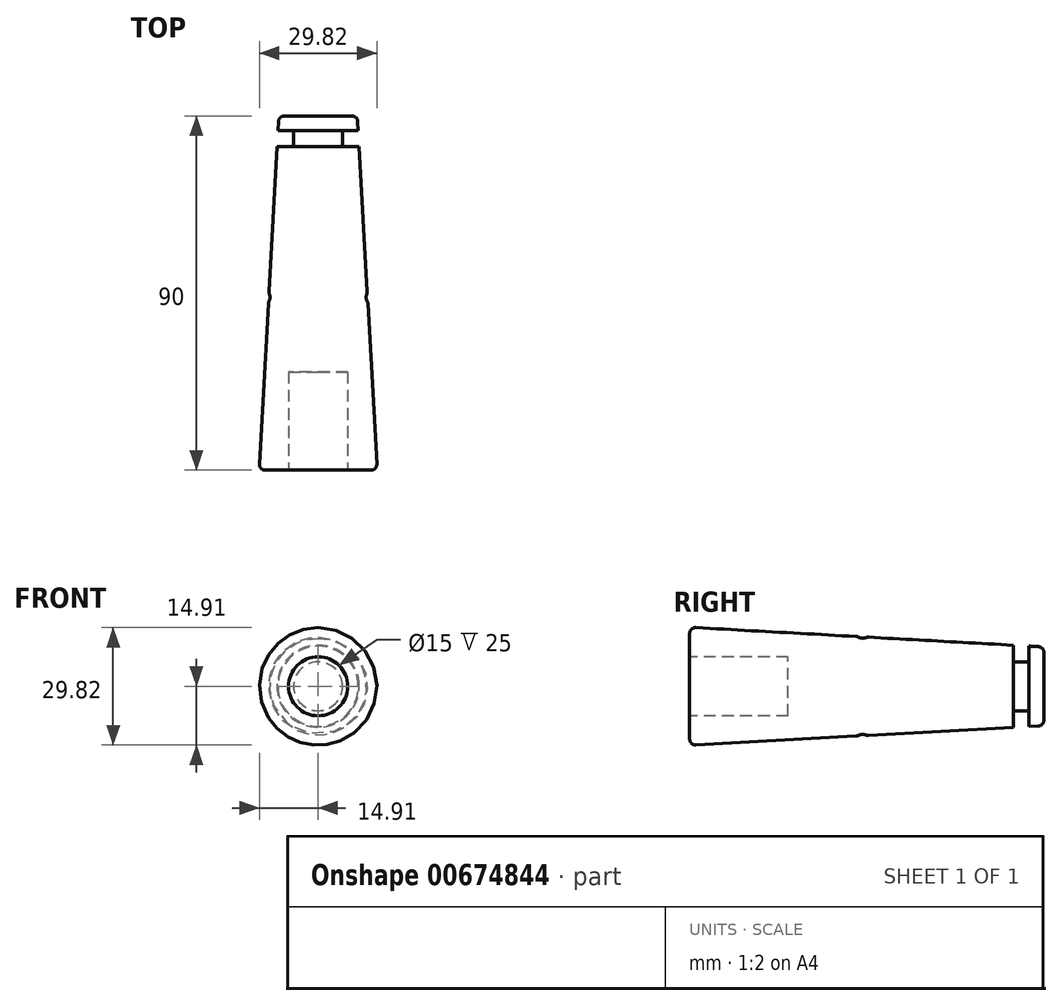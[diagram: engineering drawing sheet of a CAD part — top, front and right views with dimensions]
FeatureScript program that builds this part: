
annotation { "Feature Type Name" : "Feature", "Feature Type Description" : "" }
export const myFeature = defineFeature(function(context is Context, id is Id, definition is map)
    precondition{}
    {
        {
            var Q0;
            Q0=qCreatedBy(makeId("Top.planeOp"),FACE);
            var sketch = newSketch(context, id + "F0", { "sketchPlane" : qUnion([Q0])});
            skLineSegment(sketch, "E0.bottom", {"start": v(-7.5, 45) * mm, "end": v(2.5, 45) * mm});
            skLineSegment(sketch, "E0.top", {"start": v(-7.5, -45) * mm, "end": v(5.91, -45) * mm});
            skLineSegment(sketch, "E0.left", {"start": v(-7.5, 45) * mm, "end": v(-7.5, -45) * mm});
            skPoint(sketch, "E0.middle", {"position": v(0, 0) * mm});
            skLineSegment(sketch, "E1", {"start": v(-7.5, 45) * mm, "end": v(1.08, 45) * mm});
            skLineSegment(sketch, "E2", {"start": v(2.58, 43.58) * mm, "end": v(2.71, 41.22) * mm});
            skPoint(sketch, "E3.visualSharp", {"position": v(7.5, -45) * mm});
            skArc(sketch, "E3.filletArc", {"start": v(5.91, -45) * mm, "mid": v(7, -44.53) * mm, "end": v(7.41, -43.42) * mm});
            skPoint(sketch, "E4.visualSharp", {"position": v(2.5, 45) * mm});
            skArc(sketch, "E4.filletArc", {"start": v(2.58, 43.58) * mm, "mid": v(2.11, 44.59) * mm, "end": v(1.08, 45) * mm});
            skArc(sketch, "E5", {"start": v(4.87, -0.26) * mm, "mid": v(4.72, -1.19) * mm, "end": v(4.97, -2.1) * mm});
            skLineSegment(sketch, "E6.trimOffspring", {"start": v(5.15, -2.72) * mm, "end": v(7.41, -43.42) * mm});
            skPoint(sketch, "E7.visualSharp", {"position": v(5, 0) * mm});
            skArc(sketch, "E7.filletArc", {"start": v(4.87, -0.26) * mm, "mid": v(4.96, 0.05) * mm, "end": v(4.98, 0.38) * mm});
            skPoint(sketch, "E8.visualSharp", {"position": v(5.13, -2.34) * mm});
            skArc(sketch, "E8.filletArc", {"start": v(5.15, -2.72) * mm, "mid": v(5.1, -2.4) * mm, "end": v(4.97, -2.1) * mm});
            skLineSegment(sketch, "E9", {"start": v(2.71, 41.22) * mm, "end": v(-1.29, 41.22) * mm});
            skLineSegment(sketch, "E10", {"start": v(-1.29, 41.22) * mm, "end": v(-1.29, 37.22) * mm});
            skLineSegment(sketch, "E11", {"start": v(-1.29, 37.22) * mm, "end": v(2.93, 37.22) * mm});
            skLineSegment(sketch, "E12.trimOffspring", {"start": v(2.93, 37.22) * mm, "end": v(4.98, 0.38) * mm});
            skSolve(sketch);
        }
        {
            var Q0;
            Q0=makeQuery(id+"F0.imprint","IMPRINT",FACE,{"disambiguationData":[TD([[makeQuery(id+"F0.imprint","IMPRINT",EDGE,{"derivedFrom":sQuery(id+"F0.wireOp",EDGE,"E0.top")}),1.0]])]});
            var Q1;
            Q1=sQuery(id+"F0.wireOp",EDGE,"E0.left");
            revolve(context, id + "F1", {"entities" : qUnion([Q0]), "axis" : qUnion([Q1]), "revolveType" : RevolveType.FULL});
        }
        {
            var Q0;
            Q0=makeQuery(id+"F1.opRevolve","SWEPT_FACE",FACE,{"disambiguationData":[OSD([sQuery(id+"F0.wireOp",EDGE,"E0.top")])]});
            var sketch = newSketch(context, id + "F2", { "sketchPlane" : qUnion([Q0])});
            skCircle(sketch, "E13", {"center": v(-7.5, 0) * mm, "radius": 7.5 * mm});
            skSolve(sketch);
        }
        {
            var Q0;
            Q0 = qSketchRegion(id + "F2", true);
            extrude(context, id + "F3", {"entities" : qUnion([Q0]), "operationType" : NewBodyOperationType.REMOVE, "oppositeDirection" : true, "depth" : 25 * mm, "offsetDistance" : 25 * mm});
        }
    });
